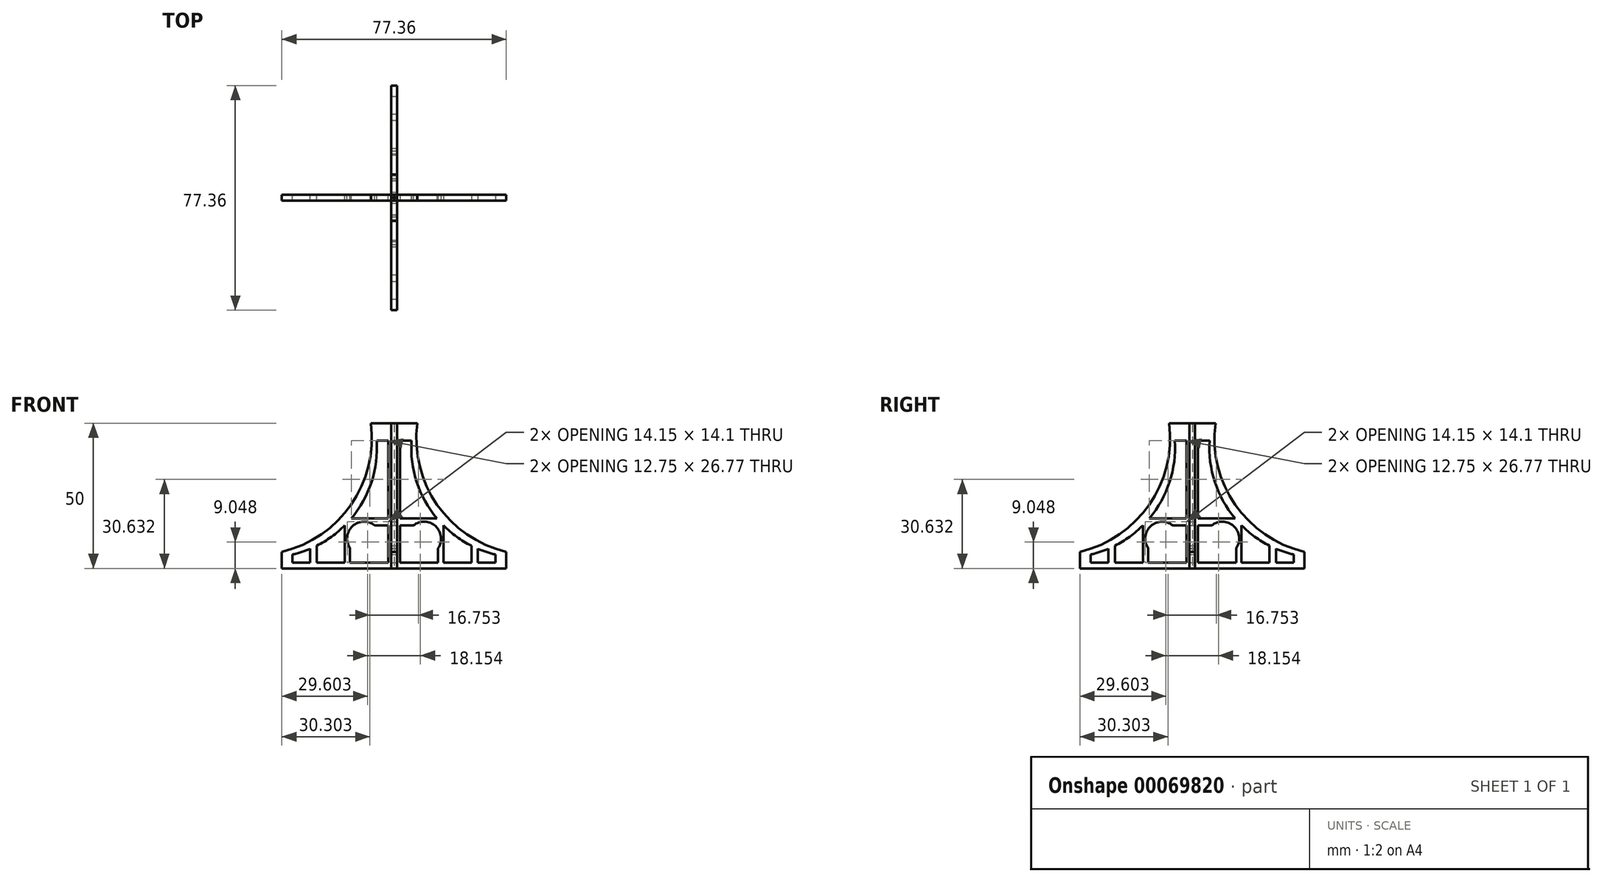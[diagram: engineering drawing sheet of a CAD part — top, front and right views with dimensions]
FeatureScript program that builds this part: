
annotation { "Feature Type Name" : "Feature", "Feature Type Description" : "" }
export const myFeature = defineFeature(function(context is Context, id is Id, definition is map)
    precondition{}
    {
        {
            var Q0;
            Q0=qCreatedBy(makeId("Right.planeOp"),FACE);
            var sketch = newSketch(context, id + "F0", { "sketchPlane" : qUnion([Q0])});
            skLineSegment(sketch, "E0", {"start": v(-8, 50) * mm, "end": v(0, 50) * mm});
            skLineSegment(sketch, "E1", {"start": v(0, 50) * mm, "end": v(0, 0) * mm});
            skLineSegment(sketch, "E2", {"start": v(0, 0) * mm, "end": v(-38.68, 0) * mm});
            skLineSegment(sketch, "E3", {"start": v(-38.68, 0) * mm, "end": v(-38.68, 5.73) * mm});
            skArc(sketch, "E4", {"start": v(-38.68, 5.73) * mm, "mid": v(-14.81, 21.95) * mm, "end": v(-8, 50) * mm});
            skLineSegment(sketch, "E5", {"start": v(-2, 44.02) * mm, "end": v(-2, 2) * mm});
            skLineSegment(sketch, "E6", {"start": v(-2, 2) * mm, "end": v(-9.1, 2) * mm});
            skLineSegment(sketch, "E7", {"start": v(-2, 44.02) * mm, "end": v(-6, 44.02) * mm});
            skLineSegment(sketch, "E8", {"start": v(-35, 2) * mm, "end": v(-35, 4.76) * mm});
            skArc(sketch, "E9", {"start": v(-35, 4.76) * mm, "mid": v(-31.91, 5.64) * mm, "end": v(-28.9, 6.77) * mm});
            skLineSegment(sketch, "E10.top", {"start": v(-26.66, 2) * mm, "end": v(-28.9, 2) * mm});
            skLineSegment(sketch, "E10.left", {"start": v(-26.66, 7.81) * mm, "end": v(-26.66, 2) * mm});
            skLineSegment(sketch, "E10.right", {"start": v(-28.9, 6.77) * mm, "end": v(-28.9, 2) * mm});
            skLineSegment(sketch, "E11.top", {"start": v(-12.03, 2) * mm, "end": v(-9.1, 2) * mm});
            skLineSegment(sketch, "E12.top", {"start": v(-17, 2) * mm, "end": v(-15.2, 2) * mm});
            skLineSegment(sketch, "E12.right", {"start": v(-17, 14.8) * mm, "end": v(-17, 2) * mm});
            skPoint(sketch, "E13.firstSnap0", {"position": v(-13.3, 17.25) * mm});
            skLineSegment(sketch, "E13.bottom", {"start": v(-14.75, 17.25) * mm, "end": v(-2, 17.25) * mm});
            skLineSegment(sketch, "E13.right", {"start": v(-2, 17.25) * mm, "end": v(-2, 14.8) * mm});
            skLineSegment(sketch, "E14.trimOffspring", {"start": v(-15.2, 6.99) * mm, "end": v(-15.2, 2) * mm});
            skLineSegment(sketch, "E15.trimOffspring", {"start": v(-6.68, 14.8) * mm, "end": v(-2, 14.8) * mm});
            skPoint(sketch, "E16.orphan", {"position": v(-17, 17.25) * mm});
            skArc(sketch, "E17.trimOffspring", {"start": v(-26.66, 7.81) * mm, "mid": v(-21.55, 10.92) * mm, "end": v(-17, 14.8) * mm});
            skArc(sketch, "E18.trimOffspring", {"start": v(-14.75, 17.25) * mm, "mid": v(-7.79, 29.79) * mm, "end": v(-6, 44.02) * mm});
            skArc(sketch, "E19.trimOffspring", {"start": v(-6.68, 14.8) * mm, "mid": v(-14.3, 14.56) * mm, "end": v(-15.2, 6.99) * mm});
            skLineSegment(sketch, "E20.trimOffspring", {"start": v(-12.03, 2) * mm, "end": v(-35, 2) * mm});
            skSolve(sketch);
        }
        {
            var Q0;
            Q0 = qSketchRegion(id + "F0", true);
            extrude(context, id + "F1", {"entities" : qUnion([Q0]), "depth" : 1 * mm, "hasSecondDirection" : true, "secondDirectionOppositeDirection" : true, "secondDirectionDepth" : 1 * mm});
        }
        {
            var Q0;
            Q0=qCreatedBy(makeId("Right.planeOp"),FACE);
            var sketch = newSketch(context, id + "F2", { "sketchPlane" : qUnion([Q0])});
            skLineSegment(sketch, "E21", {"start": v(0, 81) * mm, "end": v(0, -28.5) * mm, "construction": true});
            skSolve(sketch);
        }
        {
            var Q0;
            Q0=makeQuery(id+"F1.opExtrude","SWEPT_BODY",BODY,{"disambiguationData":[OSD([sQuery(id+"F0.wireOp",EDGE,"E0"),sQuery(id+"F0.wireOp",EDGE,"E1"),sQuery(id+"F0.wireOp",EDGE,"E2"),sQuery(id+"F0.wireOp",EDGE,"E3"),sQuery(id+"F0.wireOp",EDGE,"E4"),sQuery(id+"F0.wireOp",EDGE,"E5"),sQuery(id+"F0.wireOp",EDGE,"E6"),sQuery(id+"F0.wireOp",EDGE,"E7"),sQuery(id+"F0.wireOp",EDGE,"E8"),sQuery(id+"F0.wireOp",EDGE,"E9")])]});
            var Q1;
            Q1=sQuery(id+"F2.wireOp",EDGE,"E21");
            circularPattern(context, id + "F3", {"entities" : qUnion([Q0]), "axis" : qUnion([Q1]), "angle" : 90 * degree, "instanceCount" : 4});
        }
    });
